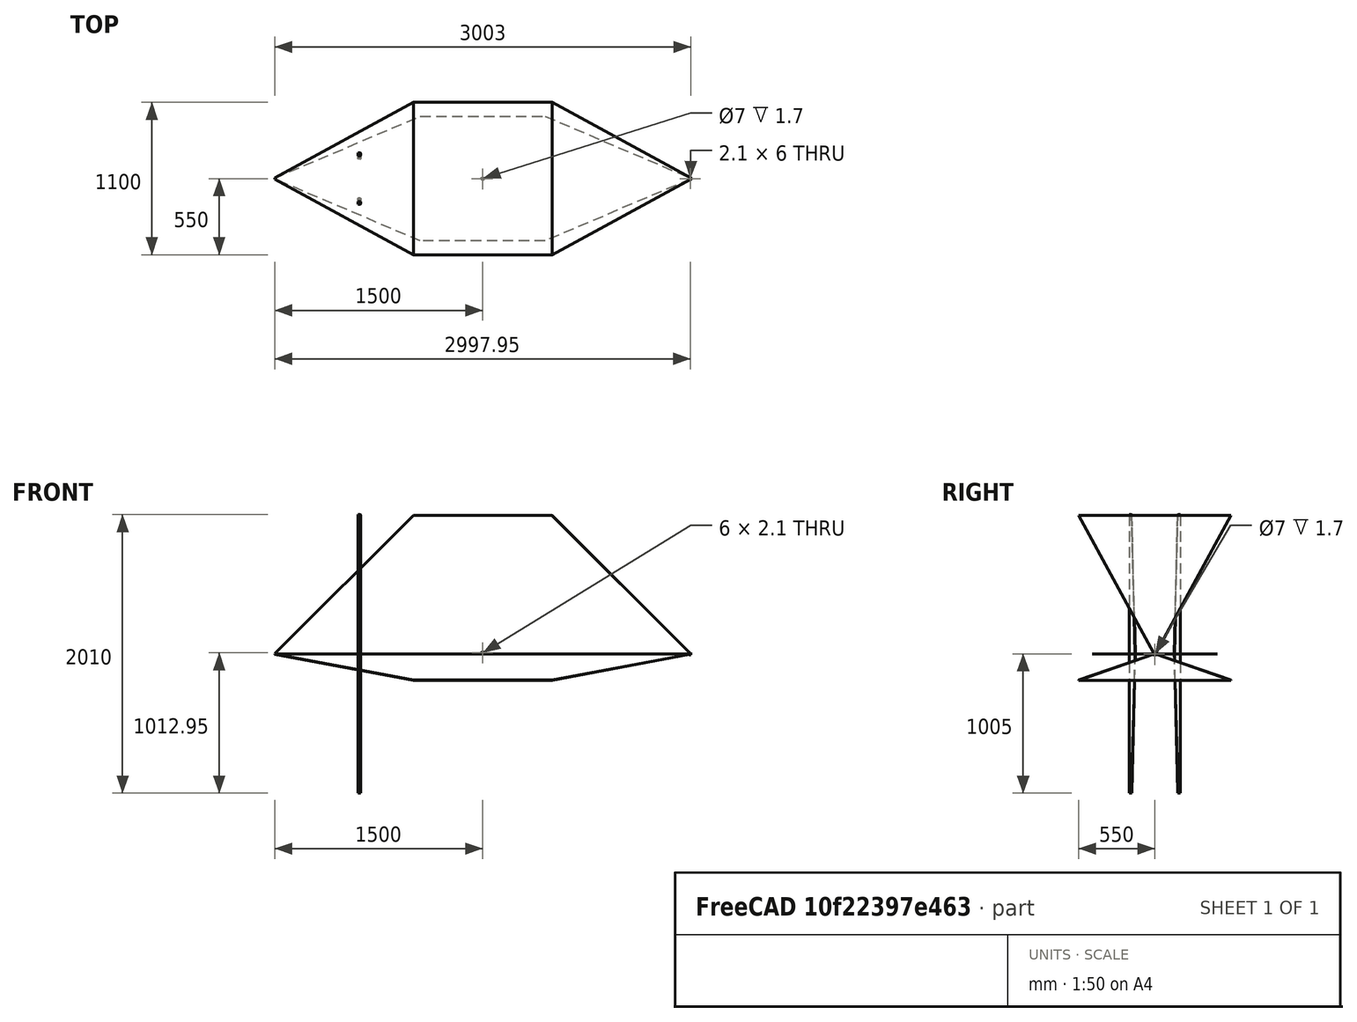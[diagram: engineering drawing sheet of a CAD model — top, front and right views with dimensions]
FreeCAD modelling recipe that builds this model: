
FCSTD DOCUMENT  (FreeCAD 0.21R33694 (Git))
Label: AsymmetricTEMCell
License: All rights reserved
LicenseURL: http://en.wikipedia.org/wiki/All_rights_reserved
objects: TechDraw::DrawViewDimension×29, Sketcher::SketchObject×8, PartDesign::Pad×6, PartDesign::Body×5, TechDraw::DrawViewPart×5, PartDesign::AdditiveWedge×5, PartDesign::Mirrored×4, Part::Mirroring×4, App::Part×3, PartDesign::SubtractiveWedge×3, PartDesign::CoordinateSystem×2, TechDraw::DrawSVGTemplate×2, TechDraw::DrawViewAnnotation×2, TechDraw::DrawPage×2, Spreadsheet::Sheet×1, PartDesign::Chamfer×1, TechDraw::DrawViewSpreadsheet×1, PartDesign::SubtractiveCylinder×1
note: 82 computed .brp shape members not serialized (recipe doc carries the construction recipe); baked Part::Feature solids carry a one-line shape summary decoded from their .brp

FEATURE [Spreadsheet::Sheet] Spreadsheet  label="Params"
  cells = A1='ShieldWidth; B1(ShieldWidth)==1100 mm; D1='Width of the outer shield sections (affects FringeCapacitance); A2='SeptumWidth; B2(SeptumWidth)==900 mm; D2='Width of the middle septum layer (affects ApproxImpedance); A3='CenterSectionLength; B3(CenterSectionLength)==1000 mm; D3='Length of the square center section of shields; A4='SeptumCenterSectionLength; B4(SeptumCenterSectionLength)==900 mm; D4='Length of the square center section of septum; A5='TaperSectionLength; B5(TaperSectionLength)==1000 mm; D5='Tapered section horizontal length of shields; A7='UpperHeight; B7(UpperHeight)==1000 mm; D7='Distance between septum and upper shield; A8='LowerHeight; B8(LowerHeight)==190 mm; D8='Distance between septum and lower shield; A10='ShieldTaperEndWidth; B10(ShieldTaperEndWidth)==12 mm; D10='For mounting the coaxial connectors (these do not significantly affect impedance); A11='ShieldTaperEndHeight; B11(ShieldTaperEndHeight)==6 mm; A12='SeptumTaperEndWidth; B12(SeptumTaperEndWidth)==6 mm; A13='MaterialThickness; B13(MaterialThickness)==1 mm; A15='Parameters below are calculated from inputs above; A17='SeptumTotalLength; B17(SeptumTotalLength)==CenterSectionLength + 2 * TaperSectionLength; D17='Total length for the middle septum layer; A18='UpperShieldTaperMaterialLength; B18(UpperShieldTaperMaterialLength)==sqrt((UpperHeight - ShieldTaperEndHeight / 2) ^ 2 + TaperSectionLength ^ 2); D18='Material length at the taper slope on each end of upper shield; A19='LowerShieldTaperMaterialLength; B19(LowerShieldTaperMaterialLength)==sqrt((LowerHeight - ShieldTaperEndHeight / 2) ^ 2 + TaperSectionLength ^ 2); A20='UpperShieldTotalLength; B20(UpperShieldTotalLength)==CenterSectionLength + UpperShieldTaperMaterialLength * 2; D20='Total material length for upper shield; A21='LowerShieldTotalLength; B21(LowerShieldTotalLength)==CenterSectionLength + LowerShieldTaperMaterialLength * 2; A22='TotalHeight; B22(TotalHeight)==UpperHeight + LowerHeight; D22='Distance between shields; A23='SeptumPosition; B23(SeptumPosition)==UpperHeight / TotalHeight; D23='0.5 for symmetric; A25='FringeCapacitance; B25(FringeCapacitance)=0.04; C25='(empirical); A26='ApproxImpedance; B26==376 / (SeptumWidth / TotalHeight * (1 / SeptumPosition + 1 / (1 - SeptumPosition)) + 4 * FringeCapacitance / 0.0885); C26='(ohm); D26='Formula according to DOI: 10.1109/TMTT.1990.4802584; A27='ApproxResonance; B27==290000 km / s / (4 * SeptumWidth); A29='UpperTaperAngle; B29(UpperTaperAngle)==atan((UpperHeight - ShieldTaperEndHeight / 2) / TaperSectionLength); A30='LowerTaperAngle; B30(LowerTaperAngle)==atan((LowerHeight - ShieldTaperEndHeight / 2) / TaperSectionLength)
FEATURE [Sketcher::SketchObject] Sketch  label="SeptumSketch"
  FullyConstrained = true
  MapMode = 5
  Support = -> [XY_Plane001]
  expr: Constraints[14] = <<Params>>.SeptumTotalLength
  expr: Constraints[15] = <<Params>>.SeptumCenterSectionLength
  expr: Constraints[16] = <<Params>>.SeptumWidth
  expr: Constraints[17] = <<Params>>.SeptumTaperEndWidth
  sketch-geometry (8):
    g0: LineSegment StartX=-1500 StartY=-3 StartZ=0 EndX=-1500 EndY=3 EndZ=0
    g1: LineSegment StartX=-1500 StartY=3 StartZ=0 EndX=-450 EndY=450 EndZ=0
    g2: LineSegment StartX=-450 StartY=450 StartZ=0 EndX=450 EndY=450 EndZ=0
    g3: LineSegment StartX=450 StartY=450 StartZ=0 EndX=1500 EndY=3 EndZ=0
    g4: LineSegment StartX=1500 StartY=3 StartZ=0 EndX=1500 EndY=-3 EndZ=0
    g5: LineSegment StartX=1500 StartY=-3 StartZ=0 EndX=450 EndY=-450 EndZ=0
    g6: LineSegment StartX=450 StartY=-450 StartZ=0 EndX=-450 EndY=-450 EndZ=0
    g7: LineSegment StartX=-450 StartY=-450 StartZ=0 EndX=-1500 EndY=-3 EndZ=0
  constraints (18):
    c: Coincident(g0,g1)
    c: Coincident(g1,g2)
    c: Coincident(g3,g4)
    c: Coincident(g4,g5)
    c: Coincident(g5,g6)
    c: Coincident(g6,g7)
    c: Coincident(g7,g0)
    c: Symmetric(g6,g1,g-1)
    c: Symmetric(g5,g2,g-1)
    c: Symmetric(g2,g1,g-2)
    c: Coincident(g3,g2)
    c: Symmetric(g3,g4,g-1)
    c: Symmetric(g4,g0,g-2)
    c: Symmetric(g0,g3,g-2)
    c: DistanceX(g0,g4) = 3000
    c: DistanceX(g2,g2) = 900
    c: DistanceY(g6,g1) = 900
    c: DistanceY(g0,g0) = 6
FEATURE [PartDesign::Pad] Pad  label="Septum001"
  Direction = (0,0,1)
  Length = 1
  Length2 = 10
  Profile = -> Sketch
  ReferenceAxis = -> Sketch [N_Axis]
  Reversed = true
  Type = 0
  expr: Length = <<Params>>.MaterialThickness
FEATURE [PartDesign::Body] Body  label="Septum"
  Group = -> [Sketch,Pad]
  Origin = -> Origin001
  Tip = -> Pad
FEATURE [Sketcher::SketchObject] Sketch001  label="UpperShieldCenterSectionSketch"
  FullyConstrained = true
  MapMode = 5
  Support = -> [XY_Plane]
  expr: Constraints[8] = <<Params>>.CenterSectionLength
  expr: Constraints[9] = <<Params>>.ShieldWidth
  sketch-geometry (4):
    g0: LineSegment StartX=-500 StartY=550 StartZ=0 EndX=500 EndY=550 EndZ=0
    g1: LineSegment StartX=500 StartY=550 StartZ=0 EndX=500 EndY=-550 EndZ=0
    g2: LineSegment StartX=500 StartY=-550 StartZ=0 EndX=-500 EndY=-550 EndZ=0
    g3: LineSegment StartX=-500 StartY=-550 StartZ=0 EndX=-500 EndY=550 EndZ=0
  constraints (11):
    c: Coincident(g0,g1)
    c: Coincident(g1,g2)
    c: Coincident(g2,g3)
    c: Coincident(g3,g0)
    c: Horizontal(g0)
    c: Horizontal(g2)
    c: Vertical(g1)
    c: Vertical(g3)
    c: DistanceX(g0,g0) = 1000
    c: DistanceY(g3,g3) = 1100
    c: Symmetric(g0,g2,g-1)
FEATURE [PartDesign::Pad] Pad001  label="UpperShieldCenterSection"
  Direction = (0,0,1)
  Length = 1
  Length2 = 10
  Profile = -> Sketch001
  ReferenceAxis = -> Sketch001 [N_Axis]
  Type = 0
  expr: Length = <<Params>>.MaterialThickness
FEATURE [PartDesign::CoordinateSystem] Local_CS  label="TaperCoordinateSystem"
  AttacherType = Attacher::AttachEngine3D
  AttachmentOffset = pos=(-500,0,0) rot=(0,1,0;0.783896rad)
  MapMode = 5
  Placement = pos=(-500,0,0) rot=(0,1,0;0.783896rad)
  Support = -> [XY_Plane]
  expr: .AttachmentOffset.Base.x = -<<Params>>.CenterSectionLength / 2
  expr: .AttachmentOffset.Rotation.Pitch = <<Params>>.UpperTaperAngle
  expr: .AttachmentOffset.Rotation.Roll = 0
FEATURE [Sketcher::SketchObject] Sketch002  label="UpperShieldTaperSectionSketch"
  FullyConstrained = true
  MapMode = 5
  Placement = pos=(-500,0,2.84e-14) rot=(0,1,0;0.783896rad)
  Support = -> [Local_CS]
  expr: .AttachmentOffset.Rotation.Angle = 0
  expr: Constraints[6] = <<Params>>.ShieldTaperEndWidth
  expr: Constraints[7] = <<Params>>.ShieldWidth
  expr: Constraints[8] = <<Params>>.UpperShieldTaperMaterialLength
  sketch-geometry (4):
    g0: LineSegment StartX=0 StartY=-550 StartZ=0 EndX=0 EndY=550 EndZ=0
    g1: LineSegment StartX=0 StartY=550 StartZ=0 EndX=-1412.09 EndY=6 EndZ=0
    g2: LineSegment StartX=-1412.09 StartY=6 StartZ=0 EndX=-1412.09 EndY=-6 EndZ=0
    g3: LineSegment StartX=-1412.09 StartY=-6 StartZ=0 EndX=0 EndY=-550 EndZ=0
  constraints (10):
    c: Coincident(g0,g1)
    c: Coincident(g1,g2)
    c: Coincident(g2,g3)
    c: Coincident(g3,g0)
    c: Symmetric(g0,g0,g-1)
    c: Symmetric(g1,g2,g-1)
    c: DistanceY(g2,g2) = 12
    c: DistanceY(g0,g0) = 1100
    c: DistanceX(g1,g0) = 1412.09
    c: PointOnObject(g0,g-2)
FEATURE [PartDesign::Pad] Pad002  label="UpperShieldTaperSection"
  BaseFeature = -> Pad001
  Direction = (0.706044,0,0.708168)
  Length = 1
  Length2 = 10
  Profile = -> Sketch002
  ReferenceAxis = -> Sketch002 [N_Axis]
  Type = 0
  expr: Length = <<Params>>.MaterialThickness
FEATURE [PartDesign::Mirrored] Mirrored  label="UpperTaperMirror"
  BaseFeature = -> Pad002
  MirrorPlane = -> YZ_Plane
  Originals = -> [Pad002]
FEATURE [PartDesign::Body] Body001  label="UpperShield"
  Group = -> [Sketch001,Pad001,Sketch002,Local_CS,Pad002,Mirrored]
  Origin = -> Origin
  Placement = pos=(0,0,1000) rot=(1,0,0;3.14159rad)
  Tip = -> Mirrored
  expr: .Placement.Base.z = <<Params>>.UpperHeight
FEATURE [PartDesign::CoordinateSystem] Local_CS001  label="TaperCoordinateSystem001"
  AttacherType = Attacher::AttachEngine3D
  AttachmentOffset = pos=(-500,0,0) rot=(0,1,0;0.184865rad)
  MapMode = 5
  Placement = pos=(-500,0,0) rot=(0,1,0;0.184865rad)
  Support = -> [XY_Plane002]
  expr: .AttachmentOffset.Base.x = -<<Params>>.CenterSectionLength / 2
  expr: .AttachmentOffset.Rotation.Pitch = <<Params>>.LowerTaperAngle
  expr: .AttachmentOffset.Rotation.Roll = 0
FEATURE [Sketcher::SketchObject] Sketch003  label="LowerShieldCenterSectionSketch"
  FullyConstrained = true
  MapMode = 5
  Support = -> [XY_Plane002]
  expr: Constraints[8] = <<Params>>.CenterSectionLength
  expr: Constraints[9] = <<Params>>.ShieldWidth
  sketch-geometry (4):
    g0: LineSegment StartX=-500 StartY=550 StartZ=0 EndX=500 EndY=550 EndZ=0
    g1: LineSegment StartX=500 StartY=550 StartZ=0 EndX=500 EndY=-550 EndZ=0
    g2: LineSegment StartX=500 StartY=-550 StartZ=0 EndX=-500 EndY=-550 EndZ=0
    g3: LineSegment StartX=-500 StartY=-550 StartZ=0 EndX=-500 EndY=550 EndZ=0
  constraints (11):
    c: Coincident(g0,g1)
    c: Coincident(g1,g2)
    c: Coincident(g2,g3)
    c: Coincident(g3,g0)
    c: Horizontal(g0)
    c: Horizontal(g2)
    c: Vertical(g1)
    c: Vertical(g3)
    c: DistanceX(g0,g0) = 1000
    c: DistanceY(g3,g3) = 1100
    c: Symmetric(g0,g2,g-1)
FEATURE [PartDesign::Pad] Pad003  label="LowerShieldCenterSection"
  Direction = (0,0,1)
  Length = 1
  Length2 = 10
  Profile = -> Sketch003
  ReferenceAxis = -> Sketch003 [N_Axis]
  Type = 0
  expr: Length = <<Params>>.MaterialThickness
FEATURE [Sketcher::SketchObject] Sketch004  label="LowerShieldTaperSectionSketch"
  FullyConstrained = true
  MapMode = 5
  Placement = pos=(-500,0,0) rot=(0,1,0;0.184865rad)
  Support = -> [Local_CS001]
  expr: .AttachmentOffset.Rotation.Angle = 0
  expr: Constraints[6] = <<Params>>.ShieldTaperEndWidth
  expr: Constraints[7] = <<Params>>.ShieldWidth
  expr: Constraints[8] = <<Params>>.LowerShieldTaperMaterialLength
  sketch-geometry (4):
    g0: LineSegment StartX=0 StartY=-550 StartZ=0 EndX=0 EndY=550 EndZ=0
    g1: LineSegment StartX=0 StartY=550 StartZ=0 EndX=-1017.33 EndY=6 EndZ=0
    g2: LineSegment StartX=-1017.33 StartY=6 StartZ=0 EndX=-1017.33 EndY=-6 EndZ=0
    g3: LineSegment StartX=-1017.33 StartY=-6 StartZ=0 EndX=0 EndY=-550 EndZ=0
  constraints (10):
    c: Coincident(g0,g1)
    c: Coincident(g1,g2)
    c: Coincident(g2,g3)
    c: Coincident(g3,g0)
    c: Symmetric(g0,g0,g-1)
    c: Symmetric(g1,g2,g-1)
    c: DistanceY(g2,g2) = 12
    c: DistanceY(g0,g0) = 1100
    c: DistanceX(g1,g0) = 1017.33
    c: PointOnObject(g0,g-2)
FEATURE [PartDesign::Pad] Pad004  label="LowerShieldTaperSection"
  BaseFeature = -> Pad003
  Direction = (0.183814,0,0.982961)
  Length = 1
  Length2 = 10
  Profile = -> Sketch004
  ReferenceAxis = -> Sketch004 [N_Axis]
  Type = 0
  expr: Length = <<Params>>.MaterialThickness
FEATURE [PartDesign::Mirrored] Mirrored001  label="LowerTaperMirror"
  BaseFeature = -> Pad004
  MirrorPlane = -> YZ_Plane002
  Originals = -> [Pad004]
FEATURE [PartDesign::Body] Body002  label="LowerShield"
  Group = -> [Sketch003,Pad003,Sketch004,Local_CS001,Pad004,Mirrored001]
  Origin = -> Origin002
  Placement = pos=(0,0,-190) rot=(1,0,0;0rad)
  Tip = -> Mirrored001
  expr: .Placement.Base.z = -<<Params>>.LowerHeight
FEATURE [Sketcher::SketchObject] Sketch006  label="SideHolderSketch"
  FullyConstrained = true
  MapMode = 5
  Support = -> [XY_Plane003]
  expr: Constraints[31] = <<Params>>.LowerHeight
  expr: Constraints[38] = (<<Params>>.ShieldWidth - <<Params>>.SeptumWidth) / 2
  expr: Constraints[40] = <<Params>>.UpperHeight
  expr: Constraints[45] = <<Params>>.MaterialThickness + 5 mm
  expr: Constraints[46] = <<Params>>.MaterialThickness + 5 mm
  sketch-geometry (16):
    g0: LineSegment StartX=0 StartY=-195 StartZ=0 EndX=0 EndY=-195 EndZ=0
    g1: LineSegment StartX=0 StartY=-195 StartZ=0 EndX=0 EndY=-190 EndZ=0
    g2: LineSegment StartX=0 StartY=-190 StartZ=0 EndX=10 EndY=-190 EndZ=0
    g3: LineSegment StartX=10 StartY=-190 StartZ=0 EndX=10 EndY=-189 EndZ=0
    g4: LineSegment StartX=10 StartY=-189 StartZ=0 EndX=0 EndY=-189 EndZ=0
    g5: LineSegment StartX=0 StartY=-189 StartZ=0 EndX=120 EndY=-1 EndZ=0
    g6: LineSegment StartX=120 StartY=-1 StartZ=0 EndX=110 EndY=-1 EndZ=0
    g7: LineSegment StartX=110 StartY=-1 StartZ=0 EndX=110 EndY=0 EndZ=0
    g8: LineSegment StartX=110 StartY=0 StartZ=0 EndX=120 EndY=0 EndZ=0
    g9: LineSegment StartX=120 StartY=0 StartZ=0 EndX=0 EndY=999 EndZ=0
    g10: LineSegment StartX=0 StartY=999 StartZ=0 EndX=10 EndY=999 EndZ=0
    g11: LineSegment StartX=10 StartY=999 StartZ=0 EndX=10 EndY=1000 EndZ=0
    g12: LineSegment StartX=10 StartY=1000 StartZ=0 EndX=0 EndY=1000 EndZ=0
    g13: LineSegment StartX=0 StartY=1000 StartZ=0 EndX=0 EndY=1005 EndZ=0
    g14: LineSegment StartX=0 StartY=1005 StartZ=0 EndX=0 EndY=1005 EndZ=0
    g15: LineSegment StartX=0 StartY=1005 StartZ=0 EndX=0 EndY=-195 EndZ=0
  constraints (48):
    c: PointOnObject(g0,g-2)
    c: Horizontal(g0)
    c: Coincident(g0,g1)
    c: Vertical(g1)
    c: Coincident(g1,g2)
    c: Horizontal(g2)
    c: Coincident(g2,g3)
    c: Vertical(g3)
    c: Coincident(g3,g4)
    c: Horizontal(g4)
    c: Coincident(g4,g5)
    c: Coincident(g5,g6)
    c: Horizontal(g6)
    c: Coincident(g6,g7)
    c: Vertical(g7)
    c: Coincident(g7,g8)
    c: Horizontal(g8)
    c: Coincident(g8,g9)
    c: Coincident(g9,g10)
    c: Horizontal(g10)
    c: Coincident(g10,g11)
    c: Vertical(g11)
    c: Coincident(g11,g12)
    c: Horizontal(g12)
    c: Coincident(g12,g13)
    c: Vertical(g13)
    c: Coincident(g13,g14)
    c: PointOnObject(g14,g-2)
    c: Horizontal(g14)
    c: Coincident(g14,g15)
    c: Coincident(g15,g0)
    c: DistanceY(g2,g-1) = 190
    c: Vertical(g1,g4)
    c: Vertical(g9,g12)
    c: Vertical(g12,g1)
    c: Vertical(g8,g5)
    c: DistanceX(g0,g2) = 10
    c: Vertical(g3,g10)
    c: DistanceX(g3,g6) = 100
    c: DistanceX(g6,g6) = 10
    c: DistanceY(g-1,g11) = 1000
    c: DistanceY(g13,g13) = 5
    c: DistanceY(g1,g1) = 5
    c: Equal(g4,g6)
    c: PointOnObject(g8,g-1)
    c: DistanceY(g10,g14) = 6
    c: DistanceY(g0,g3) = 6
    c: Equal(g3,g7)
FEATURE [PartDesign::Pad] Pad005  label="SideHolderBaseForm"
  Direction = (0,0,1)
  Length = 20
  Length2 = 10
  Profile = -> Sketch006
  ReferenceAxis = -> Sketch006 [N_Axis]
  Type = 0
FEATURE [PartDesign::Chamfer] Chamfer
  Angle = 45
  Base = -> Pad005 [Face18,Face17,Face16,Face15,Face1]
  BaseFeature = -> Pad005
  ChamferType = 0
  FlipDirection = false
  Size = 2
  Size2 = 1
  SupportTransform = false
  UseAllEdges = false
FEATURE [PartDesign::Body] Body003  label="SideHolder1"
  Group = -> [Sketch006,Pad005,Chamfer]
  Origin = -> Origin003
  Placement = pos=(880,-185,0) rot=(0.57735,0.57735,0.57735;2.0944rad)
  Tip = -> Chamfer
  expr: .Placement.Base.x = <<Params>>.SeptumCenterSectionLength / 2 - 20 mm
  expr: .Placement.Base.y = -<<Params>>.ShieldWidth / 2 - 10 mm
FEATURE [Part::Mirroring] mirror  label="SideHolder2 (mirror)"
  Base = (0,0,0)
  Normal = (1,0,0)
  Source = -> Body003
FEATURE [Part::Mirroring] mirror002  label="SideHolder4 (mirror)"
  Base = (0,0,0)
  Normal = (0,1,0)
  Source = -> Body003
FEATURE [Part::Mirroring] mirror003  label="SideHolder3 (mirror)"
  Base = (0,0,0)
  Normal = (1,0,0)
  Source = -> mirror002
FEATURE [App::Part] Part  label="SideHolders"
  Group = -> [Body003,mirror002,mirror003,mirror]
  Origin = -> Origin004
FEATURE [TechDraw::DrawSVGTemplate] Template
  Height = 297
  Orientation = 0
  Width = 210
FEATURE [TechDraw::DrawViewSpreadsheet] Sheet
  CellEnd = D27
  CellStart = A1
  Font = osifont
  LineWidth = 0.35
  LockPosition = false
  Rotation = 0
  Scale = 0.5
  ScaleType = 2
  Source = -> Spreadsheet
  Symbol = <blob: 18759 chars omitted>
  TextSize = 16
  X = 105.113
  Y = 218.016
FEATURE [TechDraw::DrawViewAnnotation] Annotation  label="Title"
  Font = osifont
  LineSpace = 80
  LockPosition = false
  MaxWidth = -1
  Rotation = 0
  Scale = 0.05
  ScaleType = 0
  Text = Asymmetric TEM cell design parameters | (generated from AsymmetricTEMCell.FCStd)
  TextSize = 5
  TextStyle = 0
  X = 100.663
  Y = 282.927
FEATURE [TechDraw::DrawSVGTemplate] Template001
  Height = 297
  Orientation = 0
  Template = <path>
  Width = 210
FEATURE [Sketcher::SketchObject] Sketch007  label="UpperShieldMaterialSketch"
  FullyConstrained = true
  expr: Constraints[14] = <<Params>>.ShieldWidth
  expr: Constraints[15] = <<Params>>.CenterSectionLength
  expr: Constraints[16] = <<Params>>.UpperShieldTaperMaterialLength
  expr: Constraints[17] = <<Params>>.ShieldTaperEndWidth
  sketch-geometry (9):
    g0: LineSegment StartX=-1912.09 StartY=-6 StartZ=0 EndX=-1912.09 EndY=6 EndZ=0
    g1: LineSegment StartX=-1912.09 StartY=6 StartZ=0 EndX=-500 EndY=550 EndZ=0
    g2: LineSegment StartX=-500 StartY=550 StartZ=0 EndX=500 EndY=550 EndZ=0
    g3: LineSegment StartX=500 StartY=550 StartZ=0 EndX=1912.09 EndY=6 EndZ=0
    g4: LineSegment StartX=1912.09 StartY=6 StartZ=0 EndX=1912.09 EndY=-6 EndZ=0
    g5: LineSegment StartX=1912.09 StartY=-6 StartZ=0 EndX=500 EndY=-550 EndZ=0
    g6: LineSegment StartX=500 StartY=-550 StartZ=0 EndX=-500 EndY=-550 EndZ=0
    g7: LineSegment StartX=-500 StartY=-550 StartZ=0 EndX=-1912.09 EndY=-6 EndZ=0
    g8: LineSegment StartX=500 StartY=550 StartZ=0 EndX=500 EndY=-550 EndZ=0
  constraints (20):
    c: Coincident(g0,g1)
    c: Coincident(g1,g2)
    c: Coincident(g2,g3)
    c: Coincident(g3,g4)
    c: Coincident(g4,g5)
    c: Coincident(g5,g6)
    c: Coincident(g6,g7)
    c: Coincident(g7,g0)
    c: Symmetric(g0,g0,g-1)
    c: Symmetric(g3,g4,g-1)
    c: Symmetric(g4,g0,g-2)
    c: Symmetric(g1,g2,g-2)
    c: Symmetric(g6,g5,g-2)
    c: Symmetric(g5,g2,g-1)
    c: DistanceY(g5,g2) = 1100
    c: DistanceX(g2,g2) = 1000
    c: DistanceX(g0,g1) = 1412.09
    c: DistanceY(g0,g0) = 12
    c: Coincident(g8,g2)
    c: Coincident(g8,g5)
FEATURE [TechDraw::DrawViewPart] View004  label="SeptumTemplate"
  CoarseView = false
  Direction = (0,0,1)
  Focus = 100
  HardHidden = false
  IsoCount = 0
  IsoHidden = false
  IsoVisible = false
  LockPosition = false
  Perspective = false
  Rotation = 0
  Scale = 0.05
  ScaleType = 0
  ScrubCount = 0
  SeamHidden = false
  SeamVisible = true
  SmoothHidden = false
  SmoothVisible = true
  Source = -> [Sketch]
  X = 103.441
  XDirection = (1,0,0)
  Y = 119.925
FEATURE [TechDraw::DrawViewDimension] Dimension019
  AngleOverride = false
  Arbitrary = false
  ArbitraryTolerances = false
  EqualTolerance = true
  ExtensionAngle = 0
  FormatSpec = %.2w
  FormatSpecOverTolerance = %+.2w
  FormatSpecUnderTolerance = %+.2w
  Inverted = false
  LineAngle = 0
  LockPosition = false
  MeasureType = 1
  OverTolerance = 0
  References2D = -> [View004]
  Rotation = 0
  Scale = 0.05
  ScaleType = 0
  TheoreticalExact = false
  Type = 2
  UnderTolerance = 0
  X = -13.331
  Y = -5.99014
FEATURE [TechDraw::DrawViewDimension] Dimension022
  AngleOverride = false
  Arbitrary = false
  ArbitraryTolerances = false
  EqualTolerance = true
  ExtensionAngle = 0
  FormatSpec = %.2w
  FormatSpecOverTolerance = %+.2w
  FormatSpecUnderTolerance = %+.2w
  Inverted = false
  LineAngle = 0
  LockPosition = false
  MeasureType = 1
  OverTolerance = 0
  References2D = -> [View004]
  Rotation = 0
  Scale = 0.05
  ScaleType = 0
  TheoreticalExact = false
  Type = 1
  UnderTolerance = 0
  X = 3.27493
  Y = 4.36951
FEATURE [PartDesign::AdditiveWedge] Wedge  label="OutsideCone"
  AttacherType = Attacher::AttachEngine3D
  MapMode = 3
  Placement = pos=(0,0,0) rot=(1,0,0;1.5708rad)
  Support = -> [XY_Plane007]
  X2max = 8
  X2min = -8
  Xmax = 12.44
  Xmin = -12.44
  Ymax = 13
  Ymin = 0
  Z2max = 8
  Z2min = -8
  Zmax = 5.87
  Zmin = -5.87
  expr: Xmax = <<Params>>.ShieldTaperEndWidth / 2 + 10 mm * (<<Params>>.ShieldWidth - <<Params>>.ShieldTaperEndWidth) / <<Params>>.TaperSectionLength / 2 + 1 mm
  expr: Xmin = -(<<Params>>.ShieldTaperEndWidth / 2 + 10 mm * (<<Params>>.ShieldWidth - <<Params>>.ShieldTaperEndWidth) / <<Params>>.TaperSectionLength / 2) - 1 mm
  expr: Zmax = <<Params>>.ShieldTaperEndHeight / 2 + 10 mm * (<<Params>>.LowerHeight - <<Params>>.ShieldTaperEndHeight / 2) / <<Params>>.TaperSectionLength + 1 mm
  expr: Zmin = -(<<Params>>.ShieldTaperEndHeight / 2 + 10 mm * (<<Params>>.LowerHeight - <<Params>>.ShieldTaperEndHeight / 2) / <<Params>>.TaperSectionLength) - 1 mm
FEATURE [PartDesign::SubtractiveWedge] Wedge001  label="InsideCone"
  AttacherType = Attacher::AttachEngine3D
  BaseFeature = -> Wedge
  MapMode = 3
  Placement = pos=(0,0,0) rot=(1,0,0;1.5708rad)
  Support = -> [XY_Plane007]
  X2max = 6
  X2min = -6
  Xmax = 11.44
  Xmin = -11.44
  Ymax = 10
  Ymin = 0
  Z2max = 3
  Z2min = -3
  Zmax = 12.97
  Zmin = -4.87
  expr: X2max = <<Params>>.ShieldTaperEndWidth / 2
  expr: X2min = -<<Params>>.ShieldTaperEndWidth / 2
  expr: Xmax = <<Params>>.ShieldTaperEndWidth / 2 + 10 mm * (<<Params>>.ShieldWidth - <<Params>>.ShieldTaperEndWidth) / <<Params>>.TaperSectionLength / 2
  expr: Xmin = -(<<Params>>.ShieldTaperEndWidth / 2 + 10 mm * (<<Params>>.ShieldWidth - <<Params>>.ShieldTaperEndWidth) / <<Params>>.TaperSectionLength / 2)
  expr: Z2max = <<Params>>.ShieldTaperEndHeight / 2
  expr: Z2min = -<<Params>>.ShieldTaperEndHeight / 2
  expr: Zmax = <<Params>>.ShieldTaperEndHeight / 2 + 10 mm * (<<Params>>.UpperHeight - <<Params>>.ShieldTaperEndHeight / 2) / <<Params>>.TaperSectionLength
  expr: Zmin = -(<<Params>>.ShieldTaperEndHeight / 2 + 10 mm * (<<Params>>.LowerHeight - <<Params>>.ShieldTaperEndHeight / 2) / <<Params>>.TaperSectionLength)
FEATURE [PartDesign::SubtractiveWedge] Wedge002  label="SMArectangle"
  AttacherType = Attacher::AttachEngine3D
  BaseFeature = -> Wedge001
  MapMode = 3
  Placement = pos=(0,0,0) rot=(1,0,0;1.5708rad)
  Support = -> [XY_Plane007]
  X2max = 6.5
  X2min = -6.5
  Xmax = 6.5
  Xmin = -6.5
  Ymax = 11
  Ymin = 0
  Z2max = 6.5
  Z2min = -6.5
  Zmax = 6.5
  Zmin = -6.5
FEATURE [PartDesign::SubtractiveCylinder] Cylinder  label="SMAhole"
  Angle = 360
  AttacherType = Attacher::AttachEngine3D
  BaseFeature = -> Wedge002
  FirstAngle = 0
  Height = 25
  MapMode = 5
  Radius = 3.5
  SecondAngle = 0
  Support = -> [XY_Plane007]
FEATURE [PartDesign::AdditiveWedge] Wedge004  label="MidHolderTop"
  AttacherType = Attacher::AttachEngine3D
  BaseFeature = -> Cylinder
  MapMode = 3
  Placement = pos=(0,0,0) rot=(1,0,0;1.5708rad)
  Support = -> [XY_Plane007]
  X2max = 9
  X2min = 8
  Xmax = 11.44
  Xmin = 8
  Ymax = 10
  Ymin = 0
  Z2max = 0
  Z2min = -1.5
  Zmax = 0
  Zmin = -1.5
  expr: Xmax = <<Params>>.ShieldTaperEndWidth / 2 + 10 mm * (<<Params>>.ShieldWidth - <<Params>>.ShieldTaperEndWidth) / <<Params>>.TaperSectionLength / 2
FEATURE [PartDesign::AdditiveWedge] Wedge005  label="MidHolderBottom"
  AttacherType = Attacher::AttachEngine3D
  BaseFeature = -> Wedge004
  MapMode = 3
  Placement = pos=(0,0,0) rot=(1,0,0;1.5708rad)
  Support = -> [XY_Plane007]
  X2max = 11
  X2min = 8
  Xmax = 11.44
  Xmin = 8
  Ymax = 10
  Ymin = 0
  Z2max = 2.5
  Z2min = 1
  Zmax = 2.5
  Zmin = 1
  expr: Xmax = <<Params>>.ShieldTaperEndWidth / 2 + 10 mm * (<<Params>>.ShieldWidth - <<Params>>.ShieldTaperEndWidth) / <<Params>>.TaperSectionLength / 2
  expr: Z2max = <<Params>>.MaterialThickness + 1.5 mm
  expr: Z2min = <<Params>>.MaterialThickness
  expr: Zmax = <<Params>>.MaterialThickness + 1.5 mm
  expr: Zmin = <<Params>>.MaterialThickness
FEATURE [PartDesign::AdditiveWedge] Wedge006  label="MidHolderSide"
  AttacherType = Attacher::AttachEngine3D
  BaseFeature = -> Wedge005
  MapMode = 3
  Placement = pos=(0,0,0) rot=(1,0,0;1.5708rad)
  Support = -> [XY_Plane007]
  X2max = 12
  X2min = 8.1
  Xmax = 11.44
  Xmin = 7.25714
  Ymax = 9
  Ymin = 0
  Z2max = 1
  Z2min = 0
  Zmax = 1
  Zmin = 0
  expr: Xmax = <<Params>>.ShieldTaperEndWidth / 2 + 10 mm * (<<Params>>.ShieldWidth - <<Params>>.ShieldTaperEndWidth) / <<Params>>.TaperSectionLength / 2
  expr: Xmin = <<Params>>.SeptumTaperEndWidth / 2 + 10 mm * (<<Params>>.SeptumWidth - <<Params>>.SeptumTaperEndWidth) / (<<Params>>.SeptumTotalLength - <<Params>>.SeptumCenterSectionLength)
  expr: Z2max = <<Params>>.MaterialThickness
  expr: Z2min = 0
  expr: Zmax = <<Params>>.MaterialThickness
  expr: Zmin = 0
FEATURE [PartDesign::Mirrored] Mirrored003  label="MidHolderMirror"
  BaseFeature = -> Wedge006
  MirrorPlane = -> YZ_Plane007
  Originals = -> [Wedge004,Wedge005,Wedge006]
  Placement = pos=(0,0,0) rot=(1,0,0;1.5708rad)
  Refine = true
FEATURE [PartDesign::SubtractiveWedge] Wedge007  label="SMAhole_printsupport"
  AttacherType = Attacher::AttachEngine3D
  BaseFeature = -> Mirrored003
  MapMode = 3
  Placement = pos=(0,0,0) rot=(1,0,0;1.5708rad)
  Support = -> [XY_Plane007]
  X2max = 6.5
  X2min = -6.5
  Xmax = 6.5
  Xmin = -6.5
  Ymax = 11.3
  Ymin = 0
  Z2max = 3.5
  Z2min = -3.5
  Zmax = 3.5
  Zmin = -3.5
FEATURE [PartDesign::AdditiveWedge] Wedge008  label="HoldWedge1"
  AttacherType = Attacher::AttachEngine3D
  BaseFeature = -> Wedge007
  MapMode = 3
  Placement = pos=(0,0,0) rot=(1,0,0;1.5708rad)
  Support = -> [XY_Plane007]
  X2max = 3
  X2min = -3
  Xmax = 3
  Xmin = -3
  Ymax = 9
  Ymin = 6.9
  Z2max = 7
  Z2min = 6
  Zmax = 7
  Zmin = 6.5
FEATURE [PartDesign::Mirrored] Mirrored002
  BaseFeature = -> Wedge008
  MirrorPlane = -> XZ_Plane007
  Originals = -> [Wedge008]
  Placement = pos=(0,0,0) rot=(1,0,0;1.5708rad)
FEATURE [PartDesign::Body] Body004  label="EndHolder001"
  Group = -> [Wedge,Wedge001,Wedge002,Cylinder,Wedge004,Wedge005,Wedge006,Mirrored003,Wedge007,Wedge008,Mirrored002]
  Origin = -> Origin007
  Tip = -> Mirrored002
FEATURE [App::Part] Part002  label="EndHolder"
  Group = -> [Body004]
  Origin = -> Origin006
  Placement = pos=(-1490,0,-5.37e-14) rot=(0.57735,-0.57735,-0.57735;2.0944rad)
  expr: .Placement.Base.x = -<<Params>>.SeptumTotalLength / 2 + 10 mm
FEATURE [Part::Mirroring] Mirror  label="EndHolder (mirrored)"
  Base = (0,0,0)
  Normal = (1,0,0)
  Source = -> Part002
FEATURE [Sketcher::SketchObject] Sketch008  label="LowerShieldMaterialSketch"
  FullyConstrained = true
  expr: Constraints[14] = <<Params>>.ShieldWidth
  expr: Constraints[15] = <<Params>>.CenterSectionLength
  expr: Constraints[16] = <<Params>>.LowerShieldTaperMaterialLength
  expr: Constraints[17] = <<Params>>.ShieldTaperEndWidth
  sketch-geometry (10):
    g0: LineSegment StartX=-1517.33 StartY=-6 StartZ=0 EndX=-1517.33 EndY=6 EndZ=0
    g1: LineSegment StartX=-1517.33 StartY=6 StartZ=0 EndX=-500 EndY=550 EndZ=0
    g2: LineSegment StartX=-500 StartY=550 StartZ=0 EndX=500 EndY=550 EndZ=0
    g3: LineSegment StartX=500 StartY=550 StartZ=0 EndX=1517.33 EndY=6 EndZ=0
    g4: LineSegment StartX=1517.33 StartY=6 StartZ=0 EndX=1517.33 EndY=-6 EndZ=0
    g5: LineSegment StartX=1517.33 StartY=-6 StartZ=0 EndX=500 EndY=-550 EndZ=0
    g6: LineSegment StartX=500 StartY=-550 StartZ=0 EndX=-500 EndY=-550 EndZ=0
    g7: LineSegment StartX=-500 StartY=-550 StartZ=0 EndX=-1517.33 EndY=-6 EndZ=0
    g8: LineSegment StartX=-500 StartY=550 StartZ=0 EndX=-500 EndY=-550 EndZ=0
    g9: LineSegment StartX=500 StartY=550 StartZ=0 EndX=500 EndY=-550 EndZ=0
  constraints (22):
    c: Coincident(g0,g1)
    c: Coincident(g1,g2)
    c: Coincident(g2,g3)
    c: Coincident(g3,g4)
    c: Coincident(g4,g5)
    c: Coincident(g5,g6)
    c: Coincident(g6,g7)
    c: Coincident(g7,g0)
    c: Symmetric(g0,g0,g-1)
    c: Symmetric(g3,g4,g-1)
    c: Symmetric(g4,g0,g-2)
    c: Symmetric(g1,g2,g-2)
    c: Symmetric(g6,g5,g-2)
    c: Symmetric(g5,g2,g-1)
    c: DistanceY(g5,g2) = 1100
    c: DistanceX(g2,g2) = 1000
    c: DistanceX(g0,g1) = 1017.33
    c: DistanceY(g0,g0) = 12
    c: Coincident(g8,g1)
    c: Coincident(g8,g6)
    c: Coincident(g9,g2)
    c: Coincident(g9,g5)
FEATURE [App::Part] Part001  label="TEMCell"
  Group = -> [Body,Body001,Body002,Sketch007,Sketch008]
  Origin = -> Origin005
FEATURE [TechDraw::DrawViewPart] View  label="SideView"
  CoarseView = true
  Direction = (0,-1,0)
  Focus = 100
  HardHidden = false
  IsoCount = 0
  IsoHidden = false
  IsoVisible = false
  LockPosition = false
  Perspective = false
  Rotation = 0
  Scale = 0.05
  ScaleType = 0
  ScrubCount = 0
  SeamHidden = false
  SeamVisible = true
  SmoothHidden = false
  SmoothVisible = true
  Source = -> [Part001]
  X = 101.882
  XDirection = (1,0,0)
  Y = 53.3787
FEATURE [TechDraw::DrawViewPart] View001  label="TopView"
  CoarseView = true
  Direction = (0,0,1)
  Focus = 100
  HardHidden = true
  IsoCount = 0
  IsoHidden = false
  IsoVisible = false
  LockPosition = false
  Perspective = false
  Rotation = 0
  Scale = 0.05
  ScaleType = 0
  ScrubCount = 0
  SeamHidden = false
  SeamVisible = true
  SmoothHidden = false
  SmoothVisible = true
  Source = -> [Part001]
  X = 101.661
  XDirection = (1,0,0)
  Y = 126.435
FEATURE [TechDraw::DrawViewDimension] Dimension
  AngleOverride = false
  Arbitrary = false
  ArbitraryTolerances = false
  EqualTolerance = true
  ExtensionAngle = 0
  FormatSpec = %.2w
  FormatSpecOverTolerance = %+.2w
  FormatSpecUnderTolerance = %+.2w
  Inverted = false
  LineAngle = 0
  LockPosition = false
  MeasureType = 1
  OverTolerance = 0
  References2D = -> [View001]
  Rotation = 0
  Scale = 0.05
  ScaleType = 0
  TheoreticalExact = false
  Type = 2
  UnderTolerance = 0
  X = 15.0813
  Y = -0.705812
FEATURE [TechDraw::DrawViewDimension] Dimension001
  AngleOverride = false
  Arbitrary = false
  ArbitraryTolerances = false
  EqualTolerance = true
  ExtensionAngle = 0
  FormatSpec = %.2w
  FormatSpecOverTolerance = %+.2w
  FormatSpecUnderTolerance = %+.2w
  Inverted = false
  LineAngle = 0
  LockPosition = false
  MeasureType = 1
  OverTolerance = 0
  References2D = -> [View001]
  Rotation = 0
  Scale = 0.05
  ScaleType = 0
  TheoreticalExact = false
  Type = 1
  UnderTolerance = 0
  X = -0.198576
  Y = -34.1588
FEATURE [TechDraw::DrawViewDimension] Dimension002
  AngleOverride = false
  Arbitrary = false
  ArbitraryTolerances = false
  EqualTolerance = true
  ExtensionAngle = 0
  FormatSpec = %.2w
  FormatSpecOverTolerance = %+.2w
  FormatSpecUnderTolerance = %+.2w
  Inverted = false
  LineAngle = 0
  LockPosition = false
  MeasureType = 1
  OverTolerance = 0
  References2D = -> [View001]
  Rotation = 0
  Scale = 0.05
  ScaleType = 0
  TheoreticalExact = false
  Type = 2
  UnderTolerance = 0
  X = -17.565
  Y = -4.55084
FEATURE [TechDraw::DrawViewDimension] Dimension003
  AngleOverride = false
  Arbitrary = false
  ArbitraryTolerances = false
  EqualTolerance = true
  ExtensionAngle = 0
  FormatSpec = %.2w
  FormatSpecOverTolerance = %+.2w
  FormatSpecUnderTolerance = %+.2w
  Inverted = false
  LineAngle = 0
  LockPosition = false
  MeasureType = 1
  OverTolerance = 0
  References2D = -> [View001]
  Rotation = 0
  Scale = 0.05
  ScaleType = 0
  TheoreticalExact = false
  Type = 1
  UnderTolerance = 0
  X = 2.59933
  Y = -28.821
FEATURE [TechDraw::DrawViewDimension] Dimension004
  AngleOverride = false
  Arbitrary = false
  ArbitraryTolerances = false
  EqualTolerance = true
  ExtensionAngle = 0
  FormatSpec = %.2w
  FormatSpecOverTolerance = %+.2w
  FormatSpecUnderTolerance = %+.2w
  Inverted = false
  LineAngle = 0
  LockPosition = false
  MeasureType = 1
  OverTolerance = 0
  References2D = -> [View001]
  Rotation = 0
  Scale = 0.05
  ScaleType = 0
  TheoreticalExact = false
  Type = 1
  UnderTolerance = 0
  X = 50.8273
  Y = -34.1899
FEATURE [TechDraw::DrawViewDimension] Dimension005
  AngleOverride = false
  Arbitrary = false
  ArbitraryTolerances = false
  EqualTolerance = true
  ExtensionAngle = 0
  FormatSpec = %.2w
  FormatSpecOverTolerance = %+.2w
  FormatSpecUnderTolerance = %+.2w
  Inverted = false
  LineAngle = 0
  LockPosition = false
  MeasureType = 1
  OverTolerance = 0
  References2D = -> [View001]
  Rotation = 0
  Scale = 0.05
  ScaleType = 0
  TheoreticalExact = false
  Type = 1
  UnderTolerance = 0
  X = -42.0502
  Y = -34.166
FEATURE [TechDraw::DrawViewDimension] Dimension006
  AngleOverride = false
  Arbitrary = false
  ArbitraryTolerances = false
  EqualTolerance = true
  ExtensionAngle = 0
  FormatSpec = %.0w
  FormatSpecOverTolerance = %+.2w
  FormatSpecUnderTolerance = %+.2w
  Inverted = false
  LineAngle = 0
  LockPosition = false
  MeasureType = 1
  OverTolerance = 0
  References2D = -> [View]
  Rotation = 0
  Scale = 0.05
  ScaleType = 0
  TheoreticalExact = false
  Type = 2
  UnderTolerance = 0
  X = -1.77143
  Y = -11.6454
FEATURE [TechDraw::DrawViewDimension] Dimension007
  AngleOverride = false
  Arbitrary = false
  ArbitraryTolerances = false
  EqualTolerance = true
  ExtensionAngle = 0
  FormatSpec = %.2w
  FormatSpecOverTolerance = %+.2w
  FormatSpecUnderTolerance = %+.2w
  Inverted = false
  LineAngle = 0
  LockPosition = false
  MeasureType = 1
  OverTolerance = 0
  References2D = -> [View]
  Rotation = 0
  Scale = 0.05
  ScaleType = 0
  TheoreticalExact = false
  Type = 2
  UnderTolerance = 0
  X = 11.2129
  Y = 6.93903
FEATURE [TechDraw::DrawViewDimension] Dimension008
  AngleOverride = false
  Arbitrary = false
  ArbitraryTolerances = false
  EqualTolerance = true
  ExtensionAngle = 0
  FormatSpec = %.0w
  FormatSpecOverTolerance = %+.2w
  FormatSpecUnderTolerance = %+.2w
  Inverted = false
  LineAngle = 0
  LockPosition = false
  MeasureType = 1
  OverTolerance = 0
  References2D = -> [View]
  Rotation = 0
  Scale = 0.05
  ScaleType = 0
  TheoreticalExact = false
  Type = 0
  UnderTolerance = 0
  X = 46.9168
  Y = 15.0217
FEATURE [TechDraw::DrawViewDimension] Dimension009
  AngleOverride = false
  Arbitrary = false
  ArbitraryTolerances = false
  EqualTolerance = true
  ExtensionAngle = 0
  FormatSpec = %.2w
  FormatSpecOverTolerance = %+.2w
  FormatSpecUnderTolerance = %+.2w
  Inverted = false
  LineAngle = 0
  LockPosition = false
  MeasureType = 1
  OverTolerance = 0
  References2D = -> [View001]
  Rotation = 0
  Scale = 0.05
  ScaleType = 0
  TheoreticalExact = false
  Type = 1
  UnderTolerance = 0
  X = -44.1761
  Y = -28.6215
FEATURE [TechDraw::DrawViewDimension] Dimension010
  AngleOverride = false
  Arbitrary = false
  ArbitraryTolerances = false
  EqualTolerance = true
  ExtensionAngle = 0
  FormatSpec = %.2w
  FormatSpecOverTolerance = %+.2w
  FormatSpecUnderTolerance = %+.2w
  Inverted = false
  LineAngle = 0
  LockPosition = false
  MeasureType = 1
  OverTolerance = 0
  References2D = -> [View001]
  Rotation = 0
  Scale = 0.05
  ScaleType = 0
  TheoreticalExact = false
  Type = 1
  UnderTolerance = 0
  X = 41.1425
  Y = -28.6215
FEATURE [TechDraw::DrawViewPart] View005  label="UpperTemplate"
  CoarseView = false
  Direction = (0,0,1)
  Focus = 100
  HardHidden = false
  IsoCount = 0
  IsoHidden = false
  IsoVisible = false
  LockPosition = false
  Perspective = false
  Rotation = 0
  Scale = 0.05
  ScaleType = 0
  ScrubCount = 0
  SeamHidden = false
  SeamVisible = true
  SmoothHidden = false
  SmoothVisible = true
  Source = -> [Sketch007]
  X = 104.248
  XDirection = (1,0,0)
  Y = 188.046
FEATURE [TechDraw::DrawViewPart] View006  label="LowerTemplate"
  CoarseView = false
  Direction = (0,0,1)
  Focus = 100
  HardHidden = false
  IsoCount = 0
  IsoHidden = false
  IsoVisible = false
  LockPosition = false
  Perspective = false
  Rotation = 0
  Scale = 0.05
  ScaleType = 0
  ScrubCount = 0
  SeamHidden = false
  SeamVisible = true
  SmoothHidden = false
  SmoothVisible = true
  Source = -> [Sketch008]
  X = 104.07
  XDirection = (1,0,0)
  Y = 50.25
FEATURE [TechDraw::DrawViewDimension] Dimension023
  AngleOverride = false
  Arbitrary = false
  ArbitraryTolerances = false
  EqualTolerance = true
  ExtensionAngle = 0
  FormatSpec = %.0w
  FormatSpecOverTolerance = %+.2w
  FormatSpecUnderTolerance = %+.2w
  Inverted = false
  LineAngle = 0
  LockPosition = false
  MeasureType = 1
  OverTolerance = 0
  References2D = -> [View005]
  Rotation = 0
  Scale = 0.05
  ScaleType = 0
  TheoreticalExact = false
  Type = 1
  UnderTolerance = 0
  X = 1.96902
  Y = 4.29418
FEATURE [TechDraw::DrawViewDimension] Dimension024
  AngleOverride = false
  Arbitrary = false
  ArbitraryTolerances = false
  EqualTolerance = true
  ExtensionAngle = 0
  FormatSpec = %.2w
  FormatSpecOverTolerance = %+.2w
  FormatSpecUnderTolerance = %+.2w
  Inverted = false
  LineAngle = 0
  LockPosition = false
  MeasureType = 1
  OverTolerance = 0
  References2D = -> [View005]
  Rotation = 0
  Scale = 0.05
  ScaleType = 0
  TheoreticalExact = false
  Type = 2
  UnderTolerance = 0
  X = -13.2998
  Y = -8.5437
FEATURE [TechDraw::DrawViewDimension] Dimension025
  AngleOverride = false
  Arbitrary = false
  ArbitraryTolerances = false
  EqualTolerance = true
  ExtensionAngle = 0
  FormatSpec = %.2w
  FormatSpecOverTolerance = %+.2w
  FormatSpecUnderTolerance = %+.2w
  Inverted = false
  LineAngle = 0
  LockPosition = false
  MeasureType = 1
  OverTolerance = 0
  References2D = -> [View006]
  Rotation = 0
  Scale = 0.05
  ScaleType = 0
  TheoreticalExact = false
  Type = 2
  UnderTolerance = 0
  X = -14.7746
  Y = -7.93358
FEATURE [TechDraw::DrawViewDimension] Dimension026
  AngleOverride = false
  Arbitrary = false
  ArbitraryTolerances = false
  EqualTolerance = true
  ExtensionAngle = 0
  FormatSpec = %.0w
  FormatSpecOverTolerance = %+.2w
  FormatSpecUnderTolerance = %+.2w
  Inverted = false
  LineAngle = 0
  LockPosition = false
  MeasureType = 1
  OverTolerance = 0
  References2D = -> [View006]
  Rotation = 0
  Scale = 0.05
  ScaleType = 0
  TheoreticalExact = false
  Type = 1
  UnderTolerance = 0
  X = -0.838746
  Y = 4.41519
FEATURE [TechDraw::DrawViewDimension] Dimension027
  AngleOverride = false
  Arbitrary = false
  ArbitraryTolerances = false
  EqualTolerance = true
  ExtensionAngle = 0
  FormatSpec = %.2w
  FormatSpecOverTolerance = %+.2w
  FormatSpecUnderTolerance = %+.2w
  Inverted = false
  LineAngle = 0
  LockPosition = false
  MeasureType = 1
  OverTolerance = 0
  References2D = -> [View005]
  Rotation = 0
  Scale = 0.05
  ScaleType = 0
  TheoreticalExact = false
  Type = 1
  UnderTolerance = 0
  X = -0.42053
  Y = 34.8874
FEATURE [TechDraw::DrawViewDimension] Dimension028
  AngleOverride = false
  Arbitrary = false
  ArbitraryTolerances = false
  EqualTolerance = true
  ExtensionAngle = 0
  FormatSpec = %.2w
  FormatSpecOverTolerance = %+.2w
  FormatSpecUnderTolerance = %+.2w
  Inverted = false
  LineAngle = 0
  LockPosition = false
  MeasureType = 1
  OverTolerance = 0
  References2D = -> [View004]
  Rotation = 0
  Scale = 0.05
  ScaleType = 0
  TheoreticalExact = false
  Type = 1
  UnderTolerance = 0
  X = -2.73344
  Y = 29.2566
FEATURE [TechDraw::DrawViewDimension] Dimension029
  AngleOverride = false
  Arbitrary = false
  ArbitraryTolerances = false
  EqualTolerance = true
  ExtensionAngle = 0
  FormatSpec = %.2w
  FormatSpecOverTolerance = %+.2w
  FormatSpecUnderTolerance = %+.2w
  Inverted = false
  LineAngle = 0
  LockPosition = false
  MeasureType = 1
  OverTolerance = 0
  References2D = -> [View006]
  Rotation = 0
  Scale = 0.05
  ScaleType = 0
  TheoreticalExact = false
  Type = 1
  UnderTolerance = 0
  X = -3.78477
  Y = 33.4156
FEATURE [TechDraw::DrawViewDimension] Dimension030
  AngleOverride = false
  Arbitrary = false
  ArbitraryTolerances = false
  EqualTolerance = true
  ExtensionAngle = 0
  FormatSpec = %.0w
  FormatSpecOverTolerance = %+.2w
  FormatSpecUnderTolerance = %+.2w
  Inverted = false
  LineAngle = 0
  LockPosition = false
  MeasureType = 1
  OverTolerance = 0
  References2D = -> [View]
  Rotation = 0
  Scale = 0.05
  ScaleType = 0
  TheoreticalExact = false
  Type = 6
  UnderTolerance = 0
  X = 24.9557
  Y = -22.794
FEATURE [TechDraw::DrawViewDimension] Dimension031
  AngleOverride = false
  Arbitrary = false
  ArbitraryTolerances = false
  EqualTolerance = true
  ExtensionAngle = 0
  FormatSpec = %.0w
  FormatSpecOverTolerance = %+.2w
  FormatSpecUnderTolerance = %+.2w
  Inverted = false
  LineAngle = 0
  LockPosition = false
  MeasureType = 1
  OverTolerance = 0
  References2D = -> [View]
  Rotation = 0
  Scale = 0.05
  ScaleType = 0
  TheoreticalExact = false
  Type = 6
  UnderTolerance = 0
  X = 22.2143
  Y = 24.6596
FEATURE [TechDraw::DrawViewDimension] Dimension032
  AngleOverride = false
  Arbitrary = false
  ArbitraryTolerances = false
  EqualTolerance = true
  ExtensionAngle = 0
  FormatSpec = %.2w
  FormatSpecOverTolerance = %+.2w
  FormatSpecUnderTolerance = %+.2w
  Inverted = false
  LineAngle = 0
  LockPosition = false
  MeasureType = 1
  OverTolerance = 0
  References2D = -> [View]
  Rotation = 0
  Scale = 0.05
  ScaleType = 0
  TheoreticalExact = false
  Type = 2
  UnderTolerance = 0
  X = -83.1807
  Y = 1.0337
FEATURE [TechDraw::DrawPage] Page  label="DimensionDrawing"
  KeepUpdated = true
  NextBalloonIndex = 5
  ProjectionType = 0
  Scale = 0.05
  Template = -> Template
  Views = -> [View,View001,Sheet,Annotation,Dimension,Dimension001,Dimension002,Dimension003,Dimension004,Dimension005,Dimension006,Dimension007,Dimension008,Dimension009,Dimension010,Dimension030,Dimension031,Dimension032]
FEATURE [TechDraw::DrawViewDimension] Dimension033
  AngleOverride = false
  Arbitrary = false
  ArbitraryTolerances = false
  EqualTolerance = true
  ExtensionAngle = 0
  FormatSpec = %.2w
  FormatSpecOverTolerance = %+.2w
  FormatSpecUnderTolerance = %+.2w
  Inverted = false
  LineAngle = 0
  LockPosition = false
  MeasureType = 1
  OverTolerance = 0
  References2D = -> [View004]
  Rotation = 0
  Scale = 0.05
  ScaleType = 0
  TheoreticalExact = false
  Type = 1
  UnderTolerance = 0
  X = 48.8437
  Y = 29.3178
FEATURE [TechDraw::DrawViewDimension] Dimension034
  AngleOverride = false
  Arbitrary = false
  ArbitraryTolerances = false
  EqualTolerance = true
  ExtensionAngle = 0
  FormatSpec = %.2w
  FormatSpecOverTolerance = %+.2w
  FormatSpecUnderTolerance = %+.2w
  Inverted = false
  LineAngle = 0
  LockPosition = false
  MeasureType = 1
  OverTolerance = 0
  References2D = -> [View004]
  Rotation = 0
  Scale = 0.05
  ScaleType = 0
  TheoreticalExact = false
  Type = 1
  UnderTolerance = 0
  X = -48.0179
  Y = 29.224
FEATURE [TechDraw::DrawViewDimension] Dimension035
  AngleOverride = false
  Arbitrary = false
  ArbitraryTolerances = false
  EqualTolerance = true
  ExtensionAngle = 0
  FormatSpec = %.0w
  FormatSpecOverTolerance = %+.2w
  FormatSpecUnderTolerance = %+.2w
  Inverted = false
  LineAngle = 0
  LockPosition = false
  MeasureType = 1
  OverTolerance = 0
  References2D = -> [View006]
  Rotation = 0
  Scale = 0.05
  ScaleType = 0
  TheoreticalExact = false
  Type = 1
  UnderTolerance = 0
  X = 50.1672
  Y = 33.4096
FEATURE [TechDraw::DrawViewDimension] Dimension036
  AngleOverride = false
  Arbitrary = false
  ArbitraryTolerances = false
  EqualTolerance = true
  ExtensionAngle = 0
  FormatSpec = %.0w
  FormatSpecOverTolerance = %+.2w
  FormatSpecUnderTolerance = %+.2w
  Inverted = false
  LineAngle = 0
  LockPosition = false
  MeasureType = 1
  OverTolerance = 0
  References2D = -> [View006]
  Rotation = 0
  Scale = 0.05
  ScaleType = 0
  TheoreticalExact = false
  Type = 1
  UnderTolerance = 0
  X = -50.664
  Y = 33.353
FEATURE [TechDraw::DrawViewDimension] Dimension037
  AngleOverride = false
  Arbitrary = false
  ArbitraryTolerances = false
  EqualTolerance = true
  ExtensionAngle = 0
  FormatSpec = %.0w
  FormatSpecOverTolerance = %+.2w
  FormatSpecUnderTolerance = %+.2w
  Inverted = false
  LineAngle = 0
  LockPosition = false
  MeasureType = 1
  OverTolerance = 0
  References2D = -> [View005]
  Rotation = 0
  Scale = 0.05
  ScaleType = 0
  TheoreticalExact = false
  Type = 1
  UnderTolerance = 0
  X = -59.7066
  Y = 34.6637
FEATURE [TechDraw::DrawViewDimension] Dimension038
  AngleOverride = false
  Arbitrary = false
  ArbitraryTolerances = false
  EqualTolerance = true
  ExtensionAngle = 0
  FormatSpec = %.0w
  FormatSpecOverTolerance = %+.2w
  FormatSpecUnderTolerance = %+.2w
  Inverted = false
  LineAngle = 0
  LockPosition = false
  MeasureType = 1
  OverTolerance = 0
  References2D = -> [View005]
  Rotation = 0
  Scale = 0.05
  ScaleType = 0
  TheoreticalExact = false
  Type = 1
  UnderTolerance = 0
  X = 61.4939
  Y = 34.4651
FEATURE [TechDraw::DrawViewAnnotation] Annotation001
  Font = osifont
  LineSpace = 100
  LockPosition = false
  MaxWidth = -1
  Rotation = 0
  Scale = 0.05
  ScaleType = 0
  Text = Dimensional drawing for cutting sheet stock.
  TextSize = 3
  TextStyle = 0
  X = 77.898
  Y = 258.481
FEATURE [TechDraw::DrawPage] Page001  label="CutTemplate"
  KeepUpdated = true
  NextBalloonIndex = 1
  ProjectionType = 0
  Scale = 0.05
  Template = -> Template001
  Views = -> [View004,Dimension019,Dimension022,View005,View006,Dimension023,Dimension024,Dimension025,Dimension026,Dimension027,Dimension028,Dimension029,Dimension033,Dimension034,Dimension035,Dimension036,Dimension037,Dimension038,Annotation001]
note: 1 file-system path scrubbed to <path> (originals preserved in the JSON sidecar)
